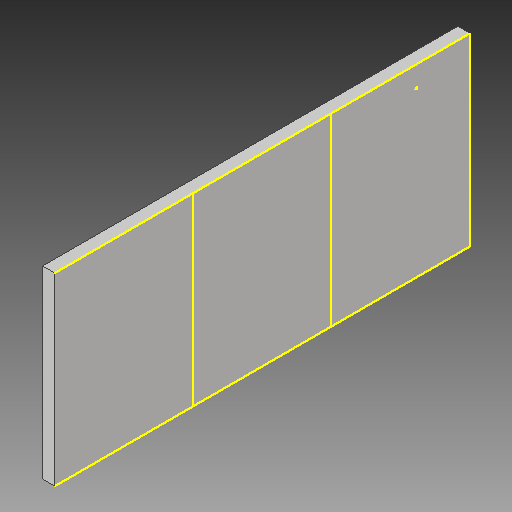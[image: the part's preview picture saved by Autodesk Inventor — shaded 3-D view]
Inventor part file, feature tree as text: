
AUTODESK INVENTOR PART (.ipt)
format: ipt  version: 2017 (Build 210142000, 142)  size: 82,432 bytes
history: native  units: in
note: dims shown in document units (in); Inventor stores cm internally (conversion verified against a paired STEP export)
features: other x3, sketch x2
ambient origin geometry x8: Origin, YZ Plane, XZ Plane, XY Plane, X Axis, Y Axis, Z Axis, Center Point
bodies: Solid1 (feature_tree)
feature tree (5):
  other  "bottom near wheel 4.5x2.ipt"
  other  "Solid1::bottom near wheel 4.5x2.ipt"
  other  "TaggingFeature1"
  sketch  "Sketch1"  dims[d0=0.3937in]
  sketch  "Sketch2"
